# Revit family: Lighting-Proiezione-GEWISS-SPATIUMPRO3-PROIETTORI-LED_OTTICA-CIRCOLARE_3MODULI
name_source: partatom
category: Apparecchi per illuminazione
units: mm (PartAtom-declared; Revit-internal decimal feet)

## family parameters
Condiviso = Sì
Host = Superficie
Punto di calcolo locali = Sì
Quota connettore circolare = Usa diametro
Sorgente d'illuminazione = Sì
Taglio con vuoti quando caricato = No
Tipo di parte = Normale

## types (1)
- Lighting-Proiezione-GEWISS-SPATIUMPRO3-PROIETTORI-LED_OTTICA-CIRCOLARE_3MODULI
    Alimentatore = Da ordinare separatamente
    Angolo inclinazione = 60.00°
    Applicazione = Interno / Esterno
    Cablaggio = Connettore stagno tra proiettore e gruppo alimentazione
    Catalogo = LIGHTING
    Classe isolamento = I
    Codice digitale univoco (Datamatrix) = Attualmente non presente
    Colore = Grigio grafite
    Contesto = Illuminazione di grandi aree
    Controllo abbagliamento e luminanza = ULOR = 0%
    Corpo = Alluminio pressofuso
    Descrizione = SPATIUM PRO 3M CL.I C1 CRI 80 5700K
    Dispositivo di protezione = Secondo driver esterno
    Durata di vita = L90B10(Tq25°C)>100.000h; L80B10(Tq25°C)>150.000h
    Efficienza luminosa (lm/W) = 106
    Emetti da lunghezza linea = 610 mm
    Failure rate alimentatore = Secondo driver esterno
    File diagramma fotometrico = generic
    Filtro dei colori = 16777215
    Finitura colore = Verniciato a polvere poliestere
    Fissaggio = Staffa
    Frequenza nominale (Hz) = Secondo driver esterno
    Garanzia = 5 anni
    Grado di protezione = IP66
    Gruppo ottico = lente T.I.R.Ex. in PMMA HT
    Guarnizioni = silicone antinvecchiamento
    IDF = 46907d55-e74c-417a-b84a-736c4dd6485b
    IDT = 5142984a-b3a2-4d0e-8cb9-9e4b26487db4
    IPEA = GRANDI AREE = A+ // AREE VERDI = A
    Immagine tipo = SPATIUMpro3.jpg
    Inclinazione = Rotazione su staffa con goniometro integrato
    Indice di resa cromatica = CRI 80
    Lugnezza massima = 74 mm
    Lumen output (lm) = 127000
    Modello = GWP3333AF857
    Norma di riferimento = EN 60598-1; EN 60598-2-5; IEC/TR 62778; EN 62493
    Ottica = Circolare 40°
    POSIZIONE = 80000
    Peso (kg): = 30
    Potenza di sistema = 1200 W
    Produttore = GEWISS S.p.A.
    Prospetto di default = 1219 mm
    Resistenza agli urti = IK08
    Scheda Tecnica = https://www.gewiss.com
    Schermo = Vetro piano extrachiaro spessore 4mm
    Sistema di controllo = Secondo driver esterno
    Sostituibilità gruppo ottico = Non disponibile
    Sostituibilità piastra di cablaggio = Si
    Superficie massima esposta al vento : = 0,36 m²
    Temperatura di colore = 5700 K
    Temperatura di esercizio = -25 +50 °C
    Tensione di alimentazione = Secondo driver esterno
    Tipo di apparecchio = Proiettore LED ad alta potenza
    Tipo di installazione e montaggio = Torrefaro - Parete
    Tipologia sorgente luminosa = LED - Non sostituibile
    Tolleranza cromatica = SDCM = 5
    URL = https://www.gewiss.com
    Vano di alimentazione = Esterno
    Variazione temperatura colore lampada con luminosità attenuata = <Nessuno>
    Versione file RFA = 21.9
    Versioni = Luce fredda 5700K
    Viti esterne = Acciaio inossidabile
    larghezza lampada = 50 mm  [stored 0.164042 ft]

note: [stored X ft] marks values corroborated as IEEE doubles in the binary element streams (Revit-internal decimal feet)
